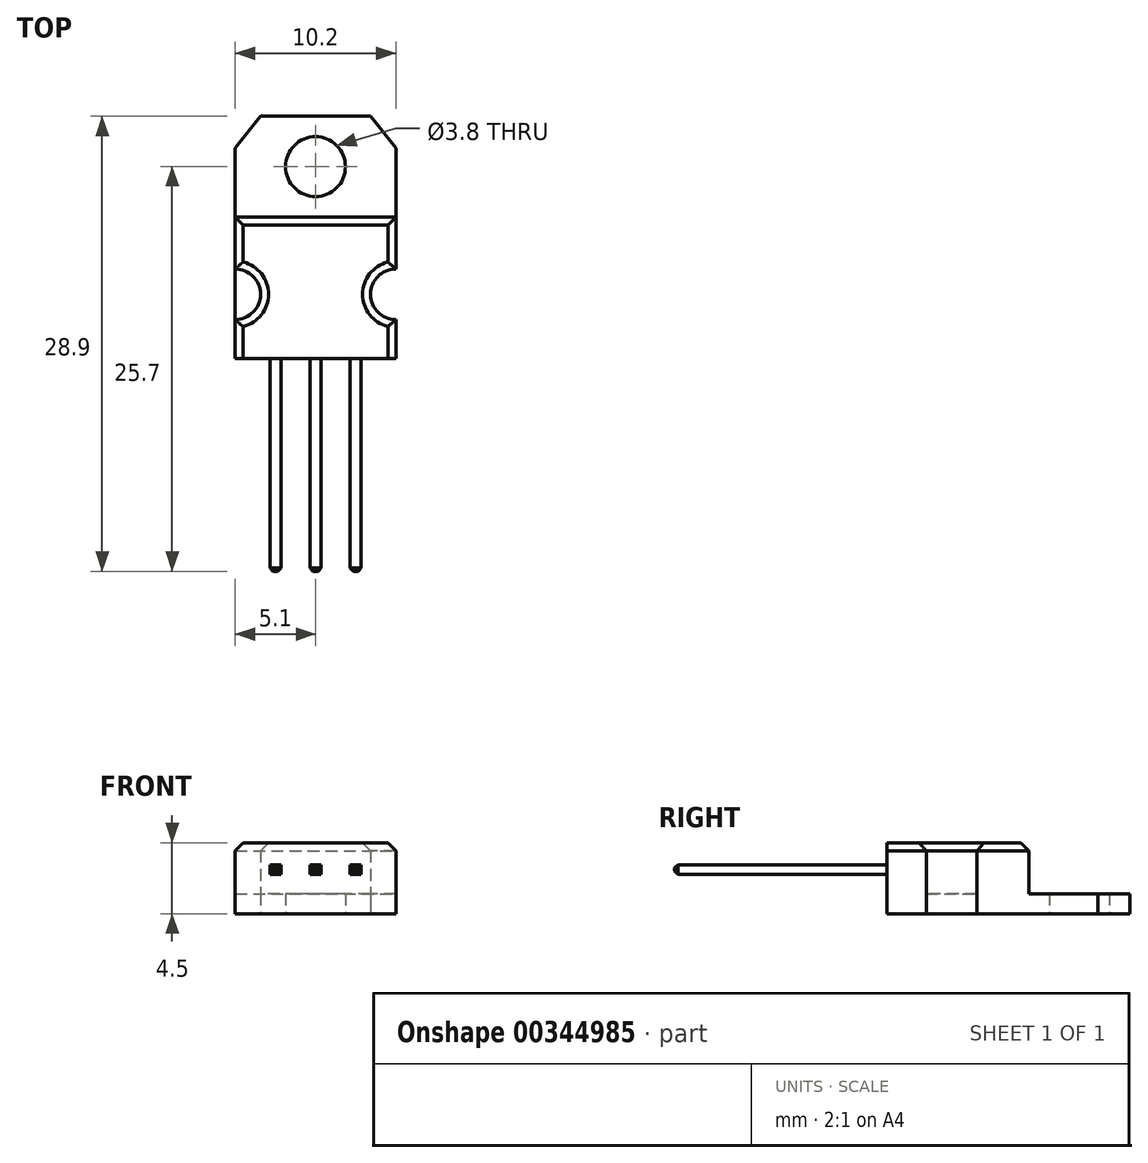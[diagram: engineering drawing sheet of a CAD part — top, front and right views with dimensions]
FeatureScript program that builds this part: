
annotation { "Feature Type Name" : "Feature", "Feature Type Description" : "" }
export const myFeature = defineFeature(function(context is Context, id is Id, definition is map)
    precondition{}
    {
        {
            var Q0;
            Q0=qCreatedBy(makeId("Top.planeOp"),FACE);
            var sketch = newSketch(context, id + "F0", { "sketchPlane" : qUnion([Q0])});
            skLineSegment(sketch, "E0.bottom", {"start": v(5.1, 7.7) * mm, "end": v(-5.1, 7.7) * mm});
            skLineSegment(sketch, "E0.top", {"start": v(5.1, -7.7) * mm, "end": v(-5.1, -7.7) * mm});
            skLineSegment(sketch, "E0.left", {"start": v(5.1, 7.7) * mm, "end": v(5.1, -7.7) * mm});
            skLineSegment(sketch, "E0.right", {"start": v(-5.1, 7.7) * mm, "end": v(-5.1, -7.7) * mm});
            skPoint(sketch, "E0.middle", {"position": v(0, 0) * mm});
            skLineSegment(sketch, "E1.bottom", {"start": v(-5.1, 7.7) * mm, "end": v(5.1, 7.7) * mm});
            skLineSegment(sketch, "E1.top", {"start": v(-5.1, 1.3) * mm, "end": v(5.1, 1.3) * mm});
            skLineSegment(sketch, "E1.left", {"start": v(-5.1, 7.7) * mm, "end": v(-5.1, 1.3) * mm});
            skLineSegment(sketch, "E1.right", {"start": v(5.1, 7.7) * mm, "end": v(5.1, 1.3) * mm});
            skCircle(sketch, "E2", {"center": v(0, 4.5) * mm, "radius": 1.9 * mm});
            skLineSegment(sketch, "E3", {"start": v(-5.1, 5.7) * mm, "end": v(-3.48, 7.7) * mm});
            skArc(sketch, "E4", {"start": v(-5.1, -5.21) * mm, "mid": v(-3.5, -3.6) * mm, "end": v(-5.1, -2) * mm});
            skArc(sketch, "E5.MirrorCS", {"start": v(5.1, -5.21) * mm, "mid": v(3.5, -3.6) * mm, "end": v(5.1, -2) * mm});
            skLineSegment(sketch, "E6.MirrorCS", {"start": v(5.1, 5.7) * mm, "end": v(3.48, 7.7) * mm});
            skSolve(sketch);
        }
        {
            var Q0;
            {var subQ2=sQuery(id+"F0.wireOp",EDGE,"E0.top");Q0=makeQuery(id+"F0.imprint","IMPRINT",FACE,{"disambiguationData":[TD([[makeQuery(id+"F0.imprint","IMPRINT",EDGE,{"derivedFrom":subQ2}),-1.0]])]});}
            extrude(context, id + "F1", {"entities" : qUnion([Q0]), "depth" : 4.5 * mm});
        }
        {
            var Q0;
            {var subQ1=sQuery(id+"F0.wireOp",EDGE,"E1.top");Q0=makeQuery(id+"F0.imprint","IMPRINT",FACE,{"disambiguationData":[TD([[makeQuery(id+"F0.imprint","IMPRINT",EDGE,{"derivedFrom":subQ1}),1.0]])]});}
            var Q1;
            {var subQ0=sQuery(id+"F0.wireOp",EDGE,"E4");Q1=makeQuery(id+"F0.imprint","IMPRINT",FACE,{"disambiguationData":[TD([[makeQuery(id+"F0.imprint","IMPRINT",EDGE,{"derivedFrom":subQ0}),1.0]])]});}
            var Q2;
            {var subQ0=sQuery(id+"F0.wireOp",EDGE,"E5.MirrorCS");Q2=makeQuery(id+"F0.imprint","IMPRINT",FACE,{"disambiguationData":[TD([[makeQuery(id+"F0.imprint","IMPRINT",EDGE,{"derivedFrom":subQ0}),-1.0]])]});}
            extrude(context, id + "F2", {"entities" : qUnion([Q0, Q1, Q2]), "operationType" : NewBodyOperationType.ADD, "depth" : 1.27 * mm});
        }
        {
            var Q0;
            {var subQ0=sQuery(id+"F0.wireOp",EDGE,"E0.right");Q0=makeQuery(id+"F1.opExtrude","CAP_EDGE",EDGE,{"disambiguationData":[OSD([subQ0]),TDD([makeQuery(id+"F0.imprint","IMPRINT",EDGE,{"disambiguationData":[TD([[makeQuery(id+"F0.imprint","INTERSECT",VERTEX,{"disambiguationData":[OD(1.0)],"derivedFrom":[subQ0,sQuery(id+"F0.wireOp",EDGE,"E4")]}),1.0]])],"derivedFrom":subQ0})])],"isStart":false});}
            var Q1;
            Q1=makeQuery(id+"F1.opExtrude","CAP_EDGE",EDGE,{"disambiguationData":[OSD([sQuery(id+"F0.wireOp",EDGE,"E1.top")])],"isStart":false});
            var Q2;
            {var subQ0=sQuery(id+"F0.wireOp",EDGE,"E0.left");Q2=makeQuery(id+"F1.opExtrude","CAP_EDGE",EDGE,{"disambiguationData":[OSD([subQ0]),TDD([makeQuery(id+"F0.imprint","IMPRINT",EDGE,{"disambiguationData":[TD([[makeQuery(id+"F0.imprint","INTERSECT",VERTEX,{"derivedFrom":[sQuery(id+"F0.wireOp",EDGE,"E1.top"),subQ0]}),-1.0]])],"derivedFrom":subQ0})])],"isStart":false});}
            var Q3;
            Q3=makeQuery(id+"F1.opExtrude","CAP_EDGE",EDGE,{"disambiguationData":[OSD([sQuery(id+"F0.wireOp",EDGE,"E5.MirrorCS")])],"isStart":false});
            var Q4;
            Q4=makeQuery(id+"F1.opExtrude","CAP_EDGE",EDGE,{"disambiguationData":[OSD([sQuery(id+"F0.wireOp",EDGE,"E4")])],"isStart":false});
            var Q5;
            {var subQ0=sQuery(id+"F0.wireOp",EDGE,"E0.right");Q5=makeQuery(id+"F1.opExtrude","CAP_EDGE",EDGE,{"disambiguationData":[OSD([subQ0]),TDD([makeQuery(id+"F0.imprint","IMPRINT",EDGE,{"disambiguationData":[TD([[makeQuery(id+"F0.imprint","INTERSECT",VERTEX,{"derivedFrom":[sQuery(id+"F0.wireOp",EDGE,"E0.top"),subQ0]}),1.0]])],"derivedFrom":subQ0})])],"isStart":false});}
            var Q6;
            {var subQ0=sQuery(id+"F0.wireOp",EDGE,"E0.left");Q6=makeQuery(id+"F1.opExtrude","CAP_EDGE",EDGE,{"disambiguationData":[OSD([subQ0]),TDD([makeQuery(id+"F0.imprint","IMPRINT",EDGE,{"disambiguationData":[TD([[makeQuery(id+"F0.imprint","INTERSECT",VERTEX,{"derivedFrom":[sQuery(id+"F0.wireOp",EDGE,"E0.top"),subQ0]}),1.0]])],"derivedFrom":subQ0})])],"isStart":false});}
            chamfer(context, id + "F3", {"entities" : qUnion([Q0, Q1, Q2, Q3, Q4, Q5, Q6]), "width" : 0.5 * mm, "tangentPropagation" : true});
        }
        {
            var Q0;
            Q0=makeQuery(id+"F1.opExtrude","SWEPT_FACE",FACE,{"disambiguationData":[OSD([sQuery(id+"F0.wireOp",EDGE,"E0.top")])]});
            var sketch = newSketch(context, id + "F4", { "sketchPlane" : qUnion([Q0])});
            skLineSegment(sketch, "E7.bottom", {"start": v(-2.2, 3.1) * mm, "end": v(-2.9, 3.1) * mm});
            skLineSegment(sketch, "E7.top", {"start": v(-2.2, 2.5) * mm, "end": v(-2.9, 2.5) * mm});
            skLineSegment(sketch, "E7.left", {"start": v(-2.2, 3.1) * mm, "end": v(-2.2, 2.5) * mm});
            skLineSegment(sketch, "E7.right", {"start": v(-2.9, 3.1) * mm, "end": v(-2.9, 2.5) * mm});
            skPoint(sketch, "E7.middle", {"position": v(-2.55, 2.8) * mm});
            skLineSegment(sketch, "E8.1.0.0", {"start": v(0.35, 3.1) * mm, "end": v(-0.35, 3.1) * mm});
            skLineSegment(sketch, "E8.1.0.1", {"start": v(0.35, 2.5) * mm, "end": v(-0.35, 2.5) * mm});
            skLineSegment(sketch, "E8.1.0.2", {"start": v(0.35, 3.1) * mm, "end": v(0.35, 2.5) * mm});
            skLineSegment(sketch, "E8.1.0.3", {"start": v(-0.35, 3.1) * mm, "end": v(-0.35, 2.5) * mm});
            skPoint(sketch, "E8.1.0.4", {"position": v(0, 2.8) * mm});
            skLineSegment(sketch, "E8.2.0.0", {"start": v(2.9, 3.1) * mm, "end": v(2.2, 3.1) * mm});
            skLineSegment(sketch, "E8.2.0.1", {"start": v(2.9, 2.5) * mm, "end": v(2.2, 2.5) * mm});
            skLineSegment(sketch, "E8.2.0.2", {"start": v(2.9, 3.1) * mm, "end": v(2.9, 2.5) * mm});
            skLineSegment(sketch, "E8.2.0.3", {"start": v(2.2, 3.1) * mm, "end": v(2.2, 2.5) * mm});
            skPoint(sketch, "E8.2.0.4", {"position": v(2.55, 2.8) * mm});
            skLineSegment(sketch, "E8.direction1", {"start": v(-2.9, 2.5) * mm, "end": v(-0.35, 2.5) * mm, "construction": true});
            skSolve(sketch);
        }
        {
            var Q0;
            Q0 = qSketchRegion(id + "F4", true);
            extrude(context, id + "F5", {"entities" : qUnion([Q0]), "operationType" : NewBodyOperationType.ADD, "depth" : 13.5 * mm});
        }
        {
            var Q0;
            Q0=makeQuery(id+"F5.opExtrude","CAP_EDGE",EDGE,{"disambiguationData":[OSD([sQuery(id+"F4.wireOp",EDGE,"E7.bottom")])],"isStart":false});
            var Q1;
            Q1=makeQuery(id+"F5.opExtrude","CAP_EDGE",EDGE,{"disambiguationData":[OSD([sQuery(id+"F4.wireOp",EDGE,"E7.right")])],"isStart":false});
            var Q2;
            Q2=makeQuery(id+"F5.opExtrude","CAP_EDGE",EDGE,{"disambiguationData":[OSD([sQuery(id+"F4.wireOp",EDGE,"E7.top")])],"isStart":false});
            var Q3;
            Q3=makeQuery(id+"F5.opExtrude","CAP_EDGE",EDGE,{"disambiguationData":[OSD([sQuery(id+"F4.wireOp",EDGE,"E7.left")])],"isStart":false});
            var Q4;
            Q4=makeQuery(id+"F5.opExtrude","CAP_EDGE",EDGE,{"disambiguationData":[OSD([sQuery(id+"F4.wireOp",EDGE,"E8.1.0.0")])],"isStart":false});
            var Q5;
            Q5=makeQuery(id+"F5.opExtrude","CAP_EDGE",EDGE,{"disambiguationData":[OSD([sQuery(id+"F4.wireOp",EDGE,"E8.1.0.3")])],"isStart":false});
            var Q6;
            Q6=makeQuery(id+"F5.opExtrude","CAP_EDGE",EDGE,{"disambiguationData":[OSD([sQuery(id+"F4.wireOp",EDGE,"E8.1.0.1")])],"isStart":false});
            var Q7;
            Q7=makeQuery(id+"F5.opExtrude","CAP_EDGE",EDGE,{"disambiguationData":[OSD([sQuery(id+"F4.wireOp",EDGE,"E8.1.0.2")])],"isStart":false});
            var Q8;
            Q8=makeQuery(id+"F5.opExtrude","CAP_EDGE",EDGE,{"disambiguationData":[OSD([sQuery(id+"F4.wireOp",EDGE,"E8.2.0.0")])],"isStart":false});
            var Q9;
            Q9=makeQuery(id+"F5.opExtrude","CAP_EDGE",EDGE,{"disambiguationData":[OSD([sQuery(id+"F4.wireOp",EDGE,"E8.2.0.3")])],"isStart":false});
            var Q10;
            Q10=makeQuery(id+"F5.opExtrude","CAP_EDGE",EDGE,{"disambiguationData":[OSD([sQuery(id+"F4.wireOp",EDGE,"E8.2.0.1")])],"isStart":false});
            var Q11;
            Q11=makeQuery(id+"F5.opExtrude","CAP_EDGE",EDGE,{"disambiguationData":[OSD([sQuery(id+"F4.wireOp",EDGE,"E8.2.0.2")])],"isStart":false});
            chamfer(context, id + "F6", {"entities" : qUnion([Q0, Q1, Q2, Q3, Q4, Q5, Q6, Q7, Q8, Q9, Q10, Q11]), "width" : 0.2 * mm, "tangentPropagation" : true});
        }
    });
